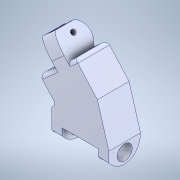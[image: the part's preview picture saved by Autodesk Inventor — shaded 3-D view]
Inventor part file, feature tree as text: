
AUTODESK INVENTOR PART (.ipt)
format: ipt  version: 2022 (Build 260153000, 153)  size: 211,456 bytes
history: mixed  units: mm
features: other x4, fillet x3, extrude x1, sketch x1, imported_body x1
ambient origin geometry x8: Origin, YZ Plane, XZ Plane, XY Plane, X Axis, Y Axis, Z Axis, Center Point
bodies: Body1 (imported_parasolid)
feature tree (10):
  other  "Sólido1"
  fillet  "Empalme1"  Radius=2.0mm
  other  "Edición directa1"
  extrude  "Extrusión1"  Depth=2.0mm TaperAngle=0.0deg
  fillet  "Empalme2"  Radius=5.2mm
  sketch  "Boceto1"  dims[d1=0.0mm d2=0.0mm d3=4.0mm d4=0.0mm d5=0.0mm d6=3.0mm d8=5.2mm d9=0.0mm d10=0.0mm d11=2.0mm d12=0.0mm d13=0.0mm d14=0.0mm]
  fillet  "Fillet1"  [1 undecoded]
  other  "Desplazar1"
  other  "Desplazar2"
  imported_body  NMx_Import_Brep_tag  [imported B-rep: ~17 faces, bbox_mm=[19.027386, 41.520021, 17.0]]
note: 1 required parameter value undecoded (feature->parameter linkage not recoverable at this tier; creation-order binding heuristic only, values carry confidence <= 0.55)
